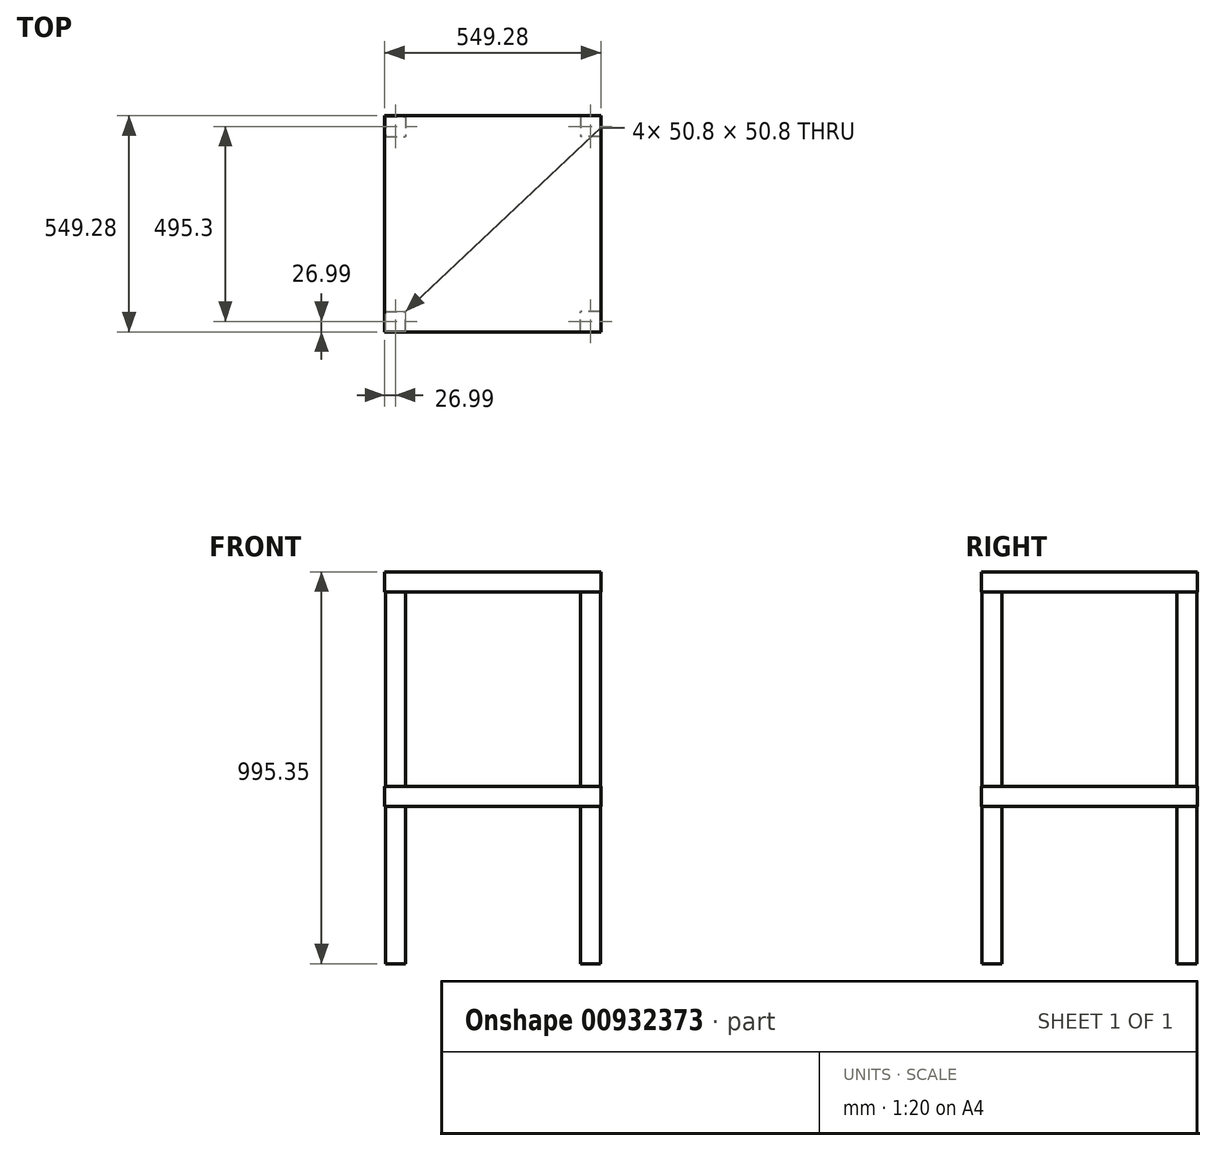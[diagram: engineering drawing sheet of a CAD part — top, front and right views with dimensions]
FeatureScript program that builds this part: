
annotation { "Feature Type Name" : "Feature", "Feature Type Description" : "" }
export const myFeature = defineFeature(function(context is Context, id is Id, definition is map)
    precondition{}
    {
        {
            var Q0;
            Q0=qCreatedBy(makeId("Top.planeOp"),FACE);
            var sketch = newSketch(context, id + "F0", { "sketchPlane" : qUnion([Q0])});
            skLineSegment(sketch, "E0.bottom", {"start": v(274.64, 274.64) * mm, "end": v(-274.64, 274.64) * mm});
            skLineSegment(sketch, "E0.top", {"start": v(274.64, -274.64) * mm, "end": v(-274.64, -274.64) * mm});
            skLineSegment(sketch, "E0.left", {"start": v(274.64, 274.64) * mm, "end": v(274.64, -274.64) * mm});
            skLineSegment(sketch, "E0.right", {"start": v(-274.64, 274.64) * mm, "end": v(-274.64, -274.64) * mm});
            skPoint(sketch, "E0.middle", {"position": v(0, 0) * mm});
            skSolve(sketch);
        }
        {
            var Q0;
            Q0 = qSketchRegion(id + "F0", true);
            extrude(context, id + "F1", {"entities" : qUnion([Q0]), "depth" : 50.8 * mm, "offsetDistance" : 25.4 * mm});
        }
        {
            var Q0;
            Q0=qCreatedBy(makeId("Top.planeOp"),FACE);
            var sketch = newSketch(context, id + "F2", { "sketchPlane" : qUnion([Q0])});
            skLineSegment(sketch, "E1.bottom", {"start": v(273.05, -273.05) * mm, "end": v(222.25, -273.05) * mm});
            skLineSegment(sketch, "E1.top", {"start": v(273.05, -222.25) * mm, "end": v(222.25, -222.25) * mm});
            skLineSegment(sketch, "E1.left", {"start": v(273.05, -273.05) * mm, "end": v(273.05, -222.25) * mm});
            skLineSegment(sketch, "E1.right", {"start": v(222.25, -273.05) * mm, "end": v(222.25, -222.25) * mm});
            skLineSegment(sketch, "E2", {"start": v(273.05, -222.25) * mm, "end": v(273.05, 0) * mm, "construction": true});
            skLineSegment(sketch, "E3", {"start": v(222.25, -273.05) * mm, "end": v(0, -273.05) * mm, "construction": true});
            skLineSegment(sketch, "E4.MirrorCS", {"start": v(222.25, 273.05) * mm, "end": v(222.25, 222.25) * mm});
            skLineSegment(sketch, "E5.MirrorCS", {"start": v(273.05, 273.05) * mm, "end": v(222.25, 273.05) * mm});
            skLineSegment(sketch, "E6.MirrorCS", {"start": v(273.05, 273.05) * mm, "end": v(273.05, 222.25) * mm});
            skLineSegment(sketch, "E7.MirrorCS", {"start": v(273.05, 222.25) * mm, "end": v(222.25, 222.25) * mm});
            skLineSegment(sketch, "E8.MirrorCS", {"start": v(-273.05, 222.25) * mm, "end": v(-222.25, 222.25) * mm});
            skLineSegment(sketch, "E9.MirrorCS", {"start": v(-273.05, -273.05) * mm, "end": v(-273.05, -222.25) * mm});
            skLineSegment(sketch, "E10.MirrorCS", {"start": v(-273.05, 273.05) * mm, "end": v(-273.05, 222.25) * mm});
            skLineSegment(sketch, "E11.MirrorCS", {"start": v(-273.05, -222.25) * mm, "end": v(-222.25, -222.25) * mm});
            skLineSegment(sketch, "E12.MirrorCS", {"start": v(-273.05, 273.05) * mm, "end": v(-222.25, 273.05) * mm});
            skLineSegment(sketch, "E13.MirrorCS", {"start": v(-273.05, -273.05) * mm, "end": v(-222.25, -273.05) * mm});
            skLineSegment(sketch, "E14.MirrorCS", {"start": v(-222.25, 273.05) * mm, "end": v(-222.25, 222.25) * mm});
            skLineSegment(sketch, "E15.MirrorCS", {"start": v(-222.25, -273.05) * mm, "end": v(-222.25, -222.25) * mm});
            skSolve(sketch);
        }
        {
            var Q0;
            Q0 = qSketchRegion(id + "F2", true);
            extrude(context, id + "F3", {"entities" : qUnion([Q0]), "operationType" : NewBodyOperationType.ADD, "oppositeDirection" : true, "depth" : 400.05 * mm, "offsetDistance" : 25.4 * mm});
        }
        {
            var Q0;
            Q0=makeQuery(id+"F1.opExtrude","SWEPT_BODY",BODY,{"disambiguationData":[OSD([sQuery(id+"F0.wireOp",EDGE,"E0.bottom"),sQuery(id+"F0.wireOp",EDGE,"E0.top"),sQuery(id+"F0.wireOp",EDGE,"E0.left"),sQuery(id+"F0.wireOp",EDGE,"E0.right")])]});
            transform(context, id + "F4", {"entities" : qUnion([Q0]), "transformType" : TransformType.TRANSLATION_3D, "dx" : 0 * mm, "dy" : 0 * mm, "dz" : -444.5 * mm - 100 * mm, "makeCopy" : true});
        }
        {
            var Q0;
            Q0 = qSketchRegion(id + "F2", true);
            var Q1;
            Q1=makeQuery(id+"F4.opPattern","COPY",BODY,{"derivedFrom":makeQuery(id+"F1.opExtrude","SWEPT_BODY",BODY,{"disambiguationData":[OSD([sQuery(id+"F0.wireOp",EDGE,"E0.bottom"),sQuery(id+"F0.wireOp",EDGE,"E0.top"),sQuery(id+"F0.wireOp",EDGE,"E0.left"),sQuery(id+"F0.wireOp",EDGE,"E0.right")])]}),"instanceName":"1"});
            extrude(context, id + "F5", {"entities" : qUnion([Q0]), "operationType" : NewBodyOperationType.ADD, "endBound" : BoundingType.UP_TO_BODY, "oppositeDirection" : true, "depth" : 25.4 * mm, "endBoundEntityBody" : qUnion([Q1]), "offsetDistance" : 400.05 * mm});
        }
    });
